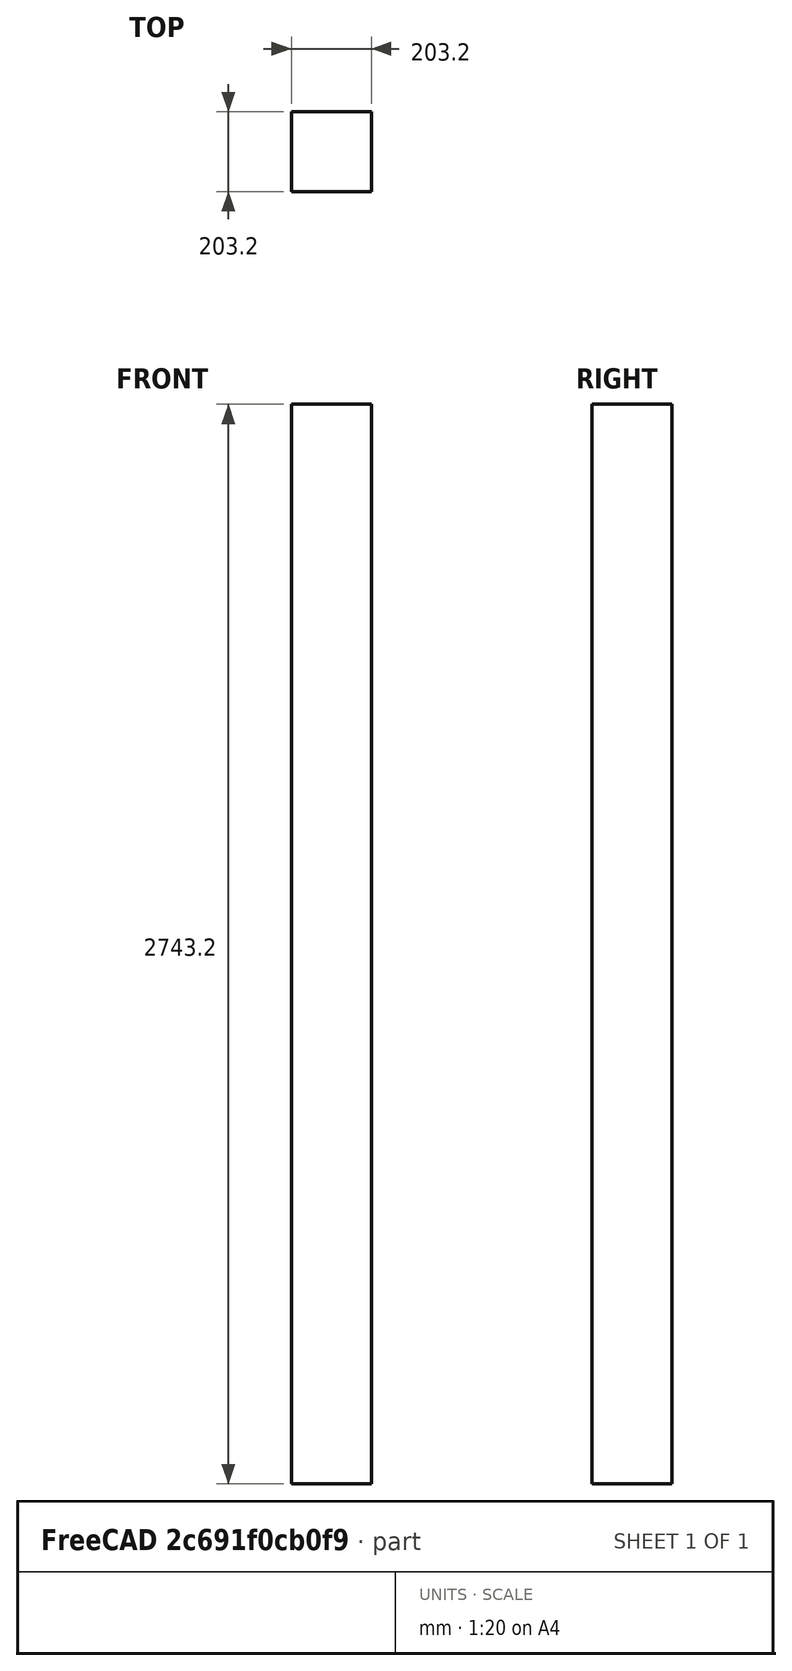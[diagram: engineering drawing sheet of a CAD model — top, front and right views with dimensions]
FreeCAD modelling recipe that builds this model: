
FCSTD DOCUMENT  (FreeCAD 0.20R29177 (Git))
Label: postEightFoot
License: All rights reserved
LicenseURL: http://en.wikipedia.org/wiki/All_rights_reserved
objects: Sketcher::SketchObject×1, PartDesign::Pad×1, PartDesign::Body×1
note: 4 computed .brp shape members not serialized (recipe doc carries the construction recipe); baked Part::Feature solids carry a one-line shape summary decoded from their .brp

FEATURE [Sketcher::SketchObject] Sketch
  FullyConstrained = true
  MapMode = 5
  Support = -> [XY_Plane]
  sketch-geometry (4):
    g0: LineSegment StartX=0 StartY=0 StartZ=0 EndX=203.2 EndY=0 EndZ=0
    g1: LineSegment StartX=203.2 StartY=0 StartZ=0 EndX=203.2 EndY=203.2 EndZ=0
    g2: LineSegment StartX=203.2 StartY=203.2 StartZ=0 EndX=0 EndY=203.2 EndZ=0
    g3: LineSegment StartX=0 StartY=203.2 StartZ=0 EndX=0 EndY=0 EndZ=0
  constraints (11):
    c: Coincident(g0,g1)
    c: Coincident(g1,g2)
    c: Coincident(g2,g3)
    c: Coincident(g3,g0)
    c: Horizontal(g0)
    c: Horizontal(g2)
    c: Vertical(g1)
    c: Vertical(g3)
    c: Coincident(g0,g-1)
    c: Equal(g3,g0)
    c: DistanceX(g0,g0) = 203.2
FEATURE [PartDesign::Pad] Pad
  Direction = (0,0,1)
  Length = 2743.2
  Length2 = 9.525
  Profile = -> Sketch
  ReferenceAxis = -> Sketch [N_Axis]
  Type = 0
FEATURE [PartDesign::Body] Body
  Group = -> [Sketch,Pad]
  Origin = -> Origin
  Tip = -> Pad
